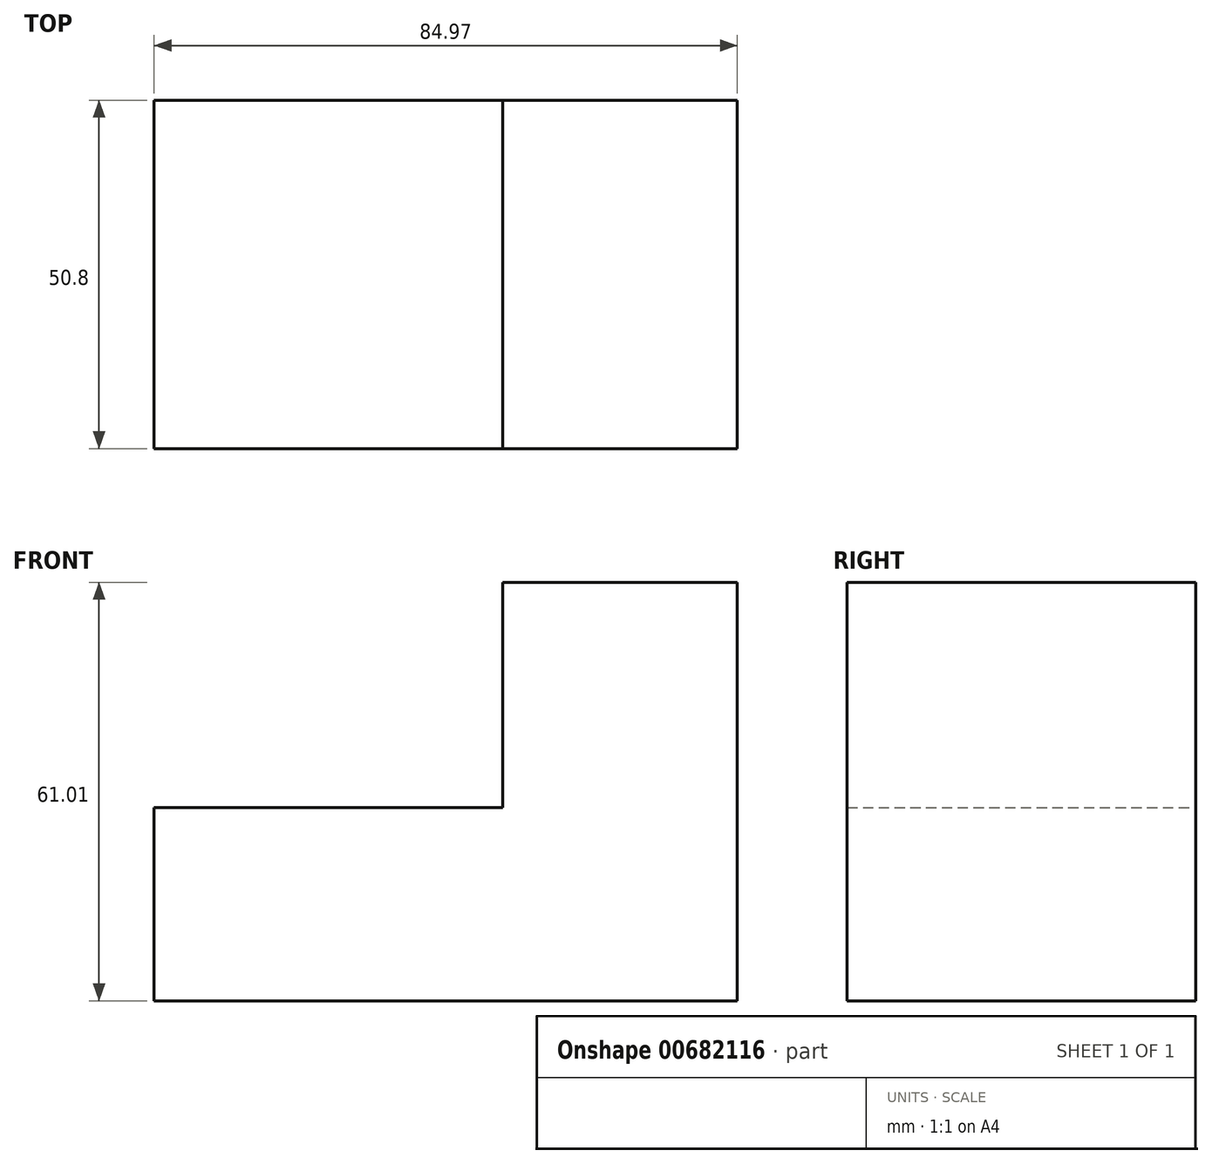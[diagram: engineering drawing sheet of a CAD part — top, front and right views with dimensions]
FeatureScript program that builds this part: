
annotation { "Feature Type Name" : "Feature", "Feature Type Description" : "" }
export const myFeature = defineFeature(function(context is Context, id is Id, definition is map)
    precondition{}
    {
        {
            var Q0;
            Q0=qCreatedBy(makeId("Front.planeOp"),FACE);
            var sketch = newSketch(context, id + "F0", { "sketchPlane" : qUnion([Q0])});
            skLineSegment(sketch, "E0", {"start": v(-45.35, 0) * mm, "end": v(-45.35, 28.17) * mm});
            skLineSegment(sketch, "E1", {"start": v(-45.35, 28.17) * mm, "end": v(5.45, 28.17) * mm});
            skLineSegment(sketch, "E2", {"start": v(5.45, 28.17) * mm, "end": v(5.45, 61.01) * mm});
            skLineSegment(sketch, "E3", {"start": v(5.45, 61.01) * mm, "end": v(39.62, 61.01) * mm});
            skLineSegment(sketch, "E4", {"start": v(39.62, 61.01) * mm, "end": v(39.62, 26.45) * mm});
            skLineSegment(sketch, "E5", {"start": v(39.62, 26.45) * mm, "end": v(39.62, 0) * mm});
            skLineSegment(sketch, "E6", {"start": v(39.62, 0) * mm, "end": v(-45.35, 0) * mm});
            skSolve(sketch);
        }
        {
            var Q0;
            Q0 = qSketchRegion(id + "F0", true);
            extrude(context, id + "F1", {"entities" : qUnion([Q0]), "depth" : 50.8 * mm, "offsetDistance" : 25.4 * mm});
        }
    });
